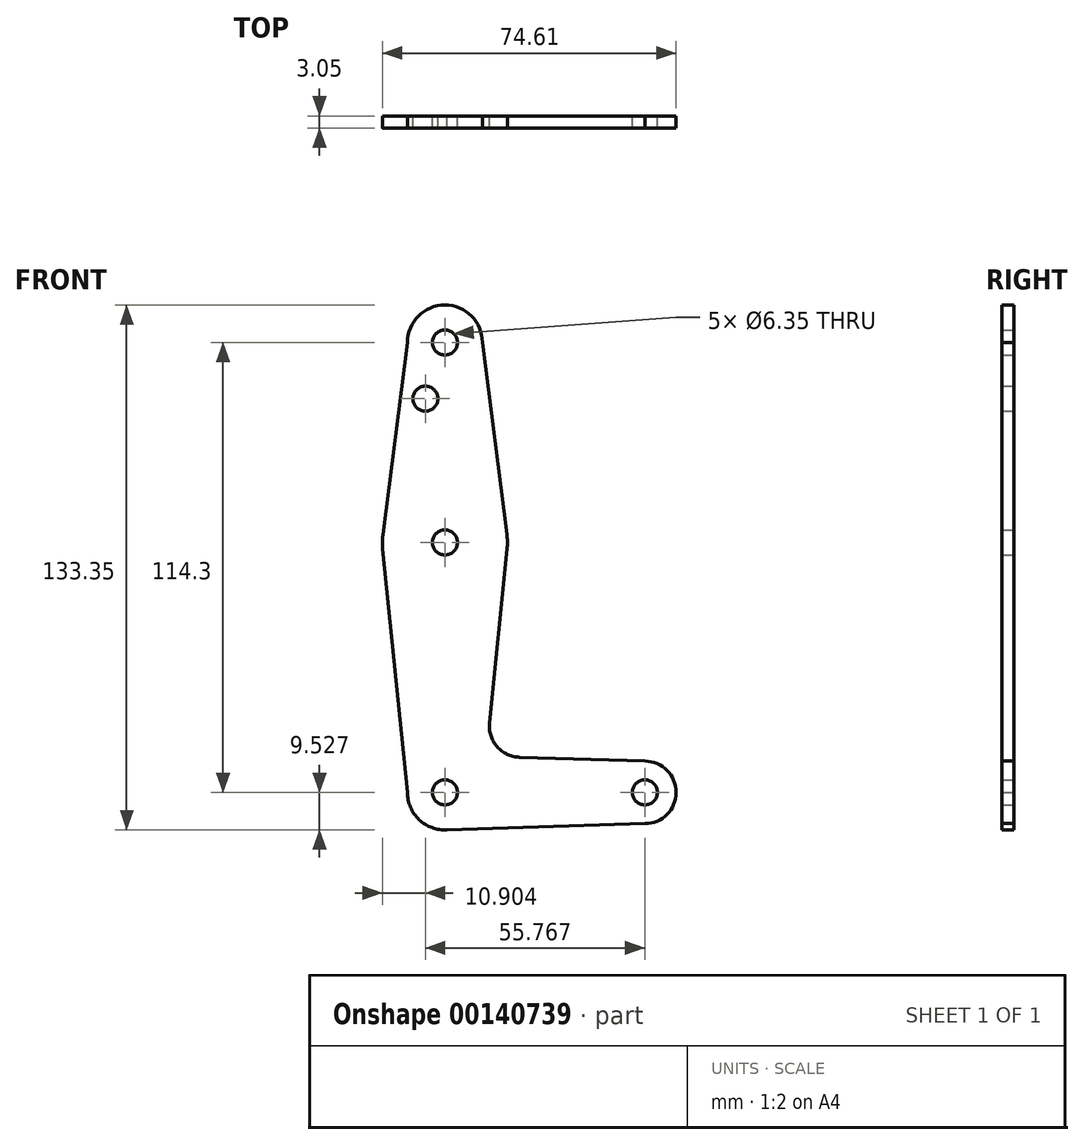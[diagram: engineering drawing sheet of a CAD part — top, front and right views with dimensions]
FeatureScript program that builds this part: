
annotation { "Feature Type Name" : "Feature", "Feature Type Description" : "" }
export const myFeature = defineFeature(function(context is Context, id is Id, definition is map)
    precondition{}
    {
        {
            var Q0;
            Q0=qCreatedBy(makeId("Front.planeOp"),FACE);
            var sketch = newSketch(context, id + "F0", { "sketchPlane" : qUnion([Q0])});
            skLineSegment(sketch, "E0", {"start": v(34.41, 66.07) * mm, "end": v(34.41, -48.23) * mm, "construction": true});
            skLineSegment(sketch, "E1", {"start": v(34.41, -48.23) * mm, "end": v(85.21, -48.23) * mm, "construction": true});
            skCircle(sketch, "E2", {"center": v(34.41, -48.23) * mm, "radius": 9.53 * mm});
            skCircle(sketch, "E3", {"center": v(85.21, -48.23) * mm, "radius": 7.94 * mm});
            skCircle(sketch, "E4", {"center": v(34.41, 66.07) * mm, "radius": 9.53 * mm});
            skCircle(sketch, "E5", {"center": v(34.41, 15.27) * mm, "radius": 15.88 * mm});
            skLineSegment(sketch, "E6", {"start": v(34.41, -57.76) * mm, "end": v(85.21, -56.17) * mm});
            skLineSegment(sketch, "E7", {"start": v(53.39, -39.3) * mm, "end": v(85.21, -40.3) * mm});
            skLineSegment(sketch, "E8", {"start": v(18.66, 17.28) * mm, "end": v(24.89, 66.07) * mm});
            skLineSegment(sketch, "E9", {"start": v(18.62, 13.67) * mm, "end": v(24.89, -48.23) * mm});
            skLineSegment(sketch, "E10", {"start": v(50.2, 13.67) * mm, "end": v(45.73, -30.55) * mm});
            skLineSegment(sketch, "E11", {"start": v(50.16, 17.28) * mm, "end": v(43.94, 66.07) * mm});
            skCircle(sketch, "E12", {"center": v(34.41, 15.27) * mm, "radius": 3.18 * mm});
            skCircle(sketch, "E13", {"center": v(29.44, 51.8) * mm, "radius": 3.18 * mm});
            skCircle(sketch, "E14", {"center": v(34.41, 66.07) * mm, "radius": 3.18 * mm});
            skCircle(sketch, "E15", {"center": v(34.41, -48.23) * mm, "radius": 3.18 * mm});
            skCircle(sketch, "E16", {"center": v(85.21, -48.23) * mm, "radius": 3.18 * mm});
            skArc(sketch, "E17.filletArc", {"start": v(45.73, -30.55) * mm, "mid": v(47.66, -36.6) * mm, "end": v(53.39, -39.3) * mm});
            skSolve(sketch);
        }
        {
            var Q0;
            Q0 = qSketchRegion(id + "F0", true);
            extrude(context, id + "F1", {"entities" : qUnion([Q0]), "depth" : 3.05 * mm});
        }
    });
